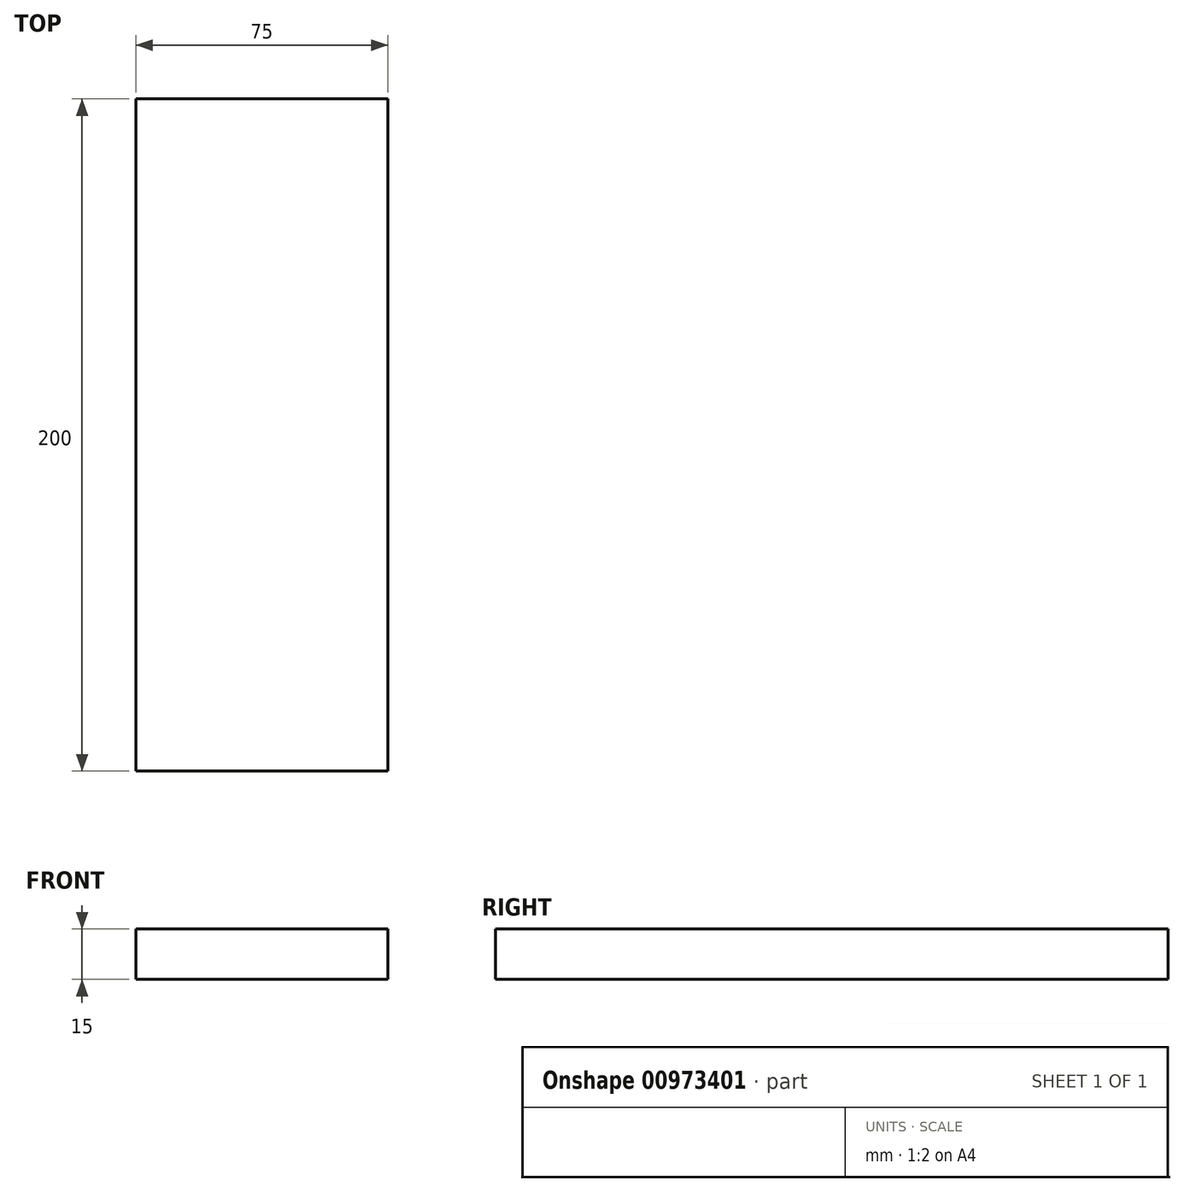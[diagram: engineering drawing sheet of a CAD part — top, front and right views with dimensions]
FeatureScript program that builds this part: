
annotation { "Feature Type Name" : "Feature", "Feature Type Description" : "" }
export const myFeature = defineFeature(function(context is Context, id is Id, definition is map)
    precondition{}
    {
        {
            var Q0;
            Q0=qCreatedBy(makeId("Top.planeOp"),FACE);
            var sketch = newSketch(context, id + "F0", { "sketchPlane" : qUnion([Q0])});
            skLineSegment(sketch, "E0.bottom", {"start": v(0, 0) * mm, "end": v(-75, 0) * mm});
            skLineSegment(sketch, "E0.top", {"start": v(0, -200) * mm, "end": v(-75, -200) * mm});
            skLineSegment(sketch, "E0.left", {"start": v(0, 0) * mm, "end": v(0, -200) * mm});
            skLineSegment(sketch, "E0.right", {"start": v(-75, 0) * mm, "end": v(-75, -200) * mm});
            skSolve(sketch);
        }
        {
            var Q0;
            Q0=makeQuery(id+"F0.imprint","IMPRINT",FACE,{"disambiguationData":[TD([[makeQuery(id+"F0.imprint","IMPRINT",EDGE,{"derivedFrom":sQuery(id+"F0.wireOp",EDGE,"E0.bottom")}),1.0]])]});
            extrude(context, id + "F1", {"entities" : qUnion([Q0]), "depth" : 15 * mm, "offsetDistance" : 25 * mm});
        }
    });
